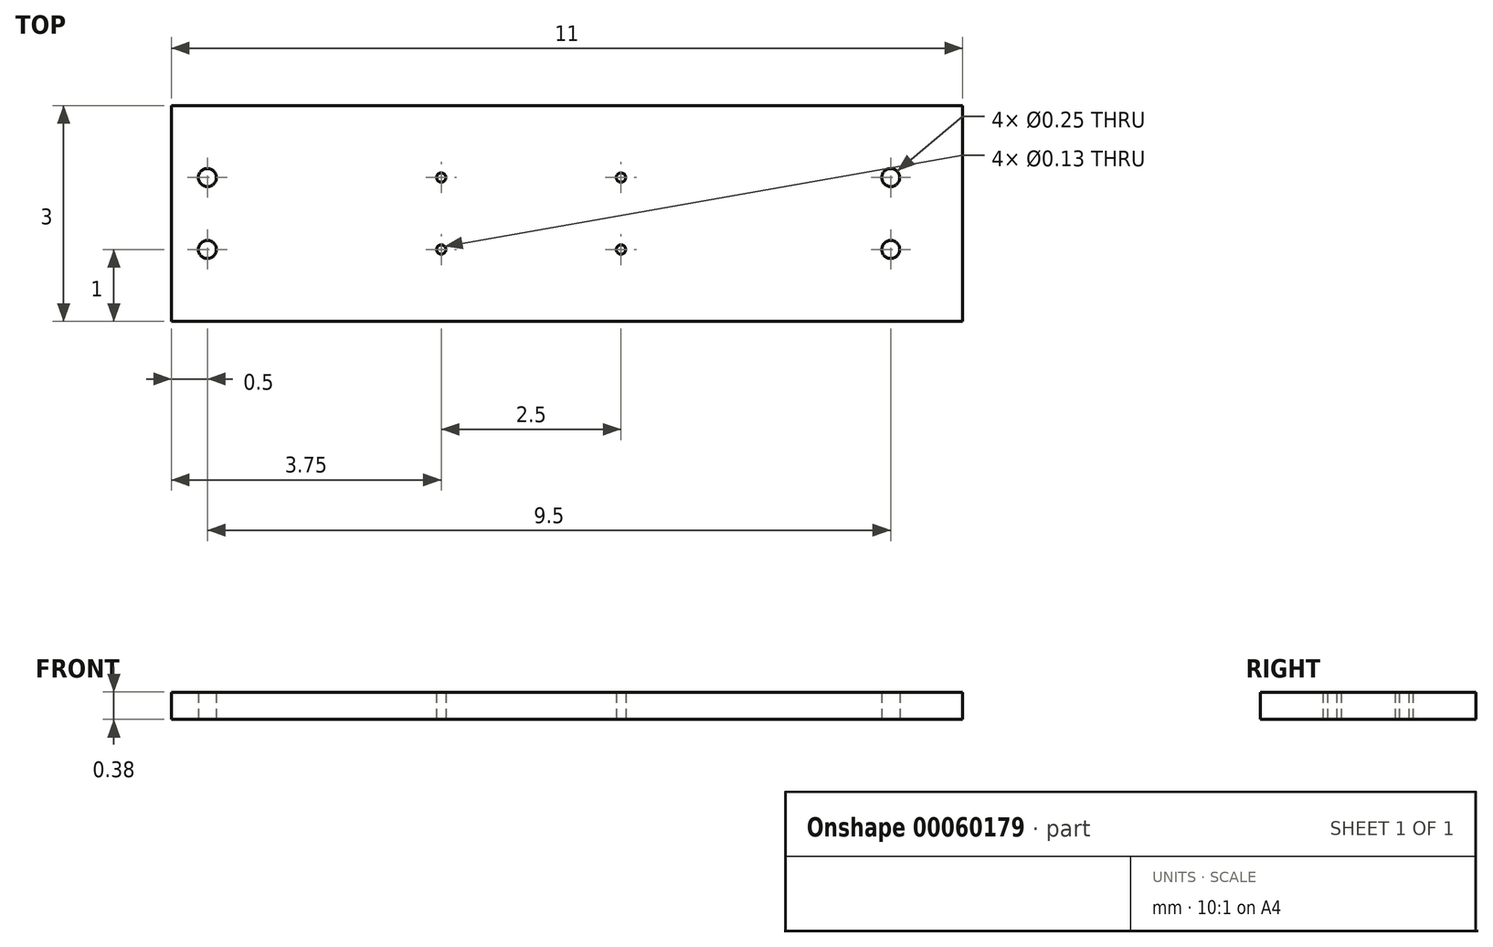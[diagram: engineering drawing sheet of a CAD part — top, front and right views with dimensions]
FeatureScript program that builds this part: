
annotation { "Feature Type Name" : "Feature", "Feature Type Description" : "" }
export const myFeature = defineFeature(function(context is Context, id is Id, definition is map)
    precondition{}
    {
        {
            var Q0;
            Q0=qCreatedBy(makeId("Top.planeOp"),FACE);
            var sketch = newSketch(context, id + "F0", { "sketchPlane" : qUnion([Q0])});
            skLineSegment(sketch, "E0.bottom", {"start": v(-5.5, 1.5) * mm, "end": v(5.5, 1.5) * mm});
            skLineSegment(sketch, "E0.top", {"start": v(-5.5, -1.5) * mm, "end": v(5.5, -1.5) * mm});
            skLineSegment(sketch, "E0.left", {"start": v(-5.5, 1.5) * mm, "end": v(-5.5, -1.5) * mm});
            skLineSegment(sketch, "E0.right", {"start": v(5.5, 1.5) * mm, "end": v(5.5, -1.5) * mm});
            skCircle(sketch, "E1", {"center": v(-5, 0.5) * mm, "radius": 0.12 * mm});
            skCircle(sketch, "E2", {"center": v(-5, -0.5) * mm, "radius": 0.12 * mm});
            skCircle(sketch, "E3", {"center": v(-1.75, 0.5) * mm, "radius": 0.07 * mm});
            skCircle(sketch, "E4", {"center": v(-1.75, -0.5) * mm, "radius": 0.07 * mm});
            skCircle(sketch, "E5", {"center": v(0.75, 0.5) * mm, "radius": 0.07 * mm});
            skCircle(sketch, "E6", {"center": v(0.75, -0.5) * mm, "radius": 0.07 * mm});
            skCircle(sketch, "E7", {"center": v(4.5, 0.5) * mm, "radius": 0.12 * mm});
            skCircle(sketch, "E8", {"center": v(4.5, -0.5) * mm, "radius": 0.12 * mm});
            skSolve(sketch);
        }
        {
            var Q0;
            Q0=makeQuery(id+"F0.imprint","IMPRINT",FACE,{"disambiguationData":[TD([[makeQuery(id+"F0.imprint","IMPRINT",EDGE,{"derivedFrom":sQuery(id+"F0.wireOp",EDGE,"E0.bottom")}),-1.0]])]});
            extrude(context, id + "F1", {"entities" : qUnion([Q0]), "endBound" : BoundingType.SYMMETRIC, "depth" : 0.38 * mm});
        }
    });
